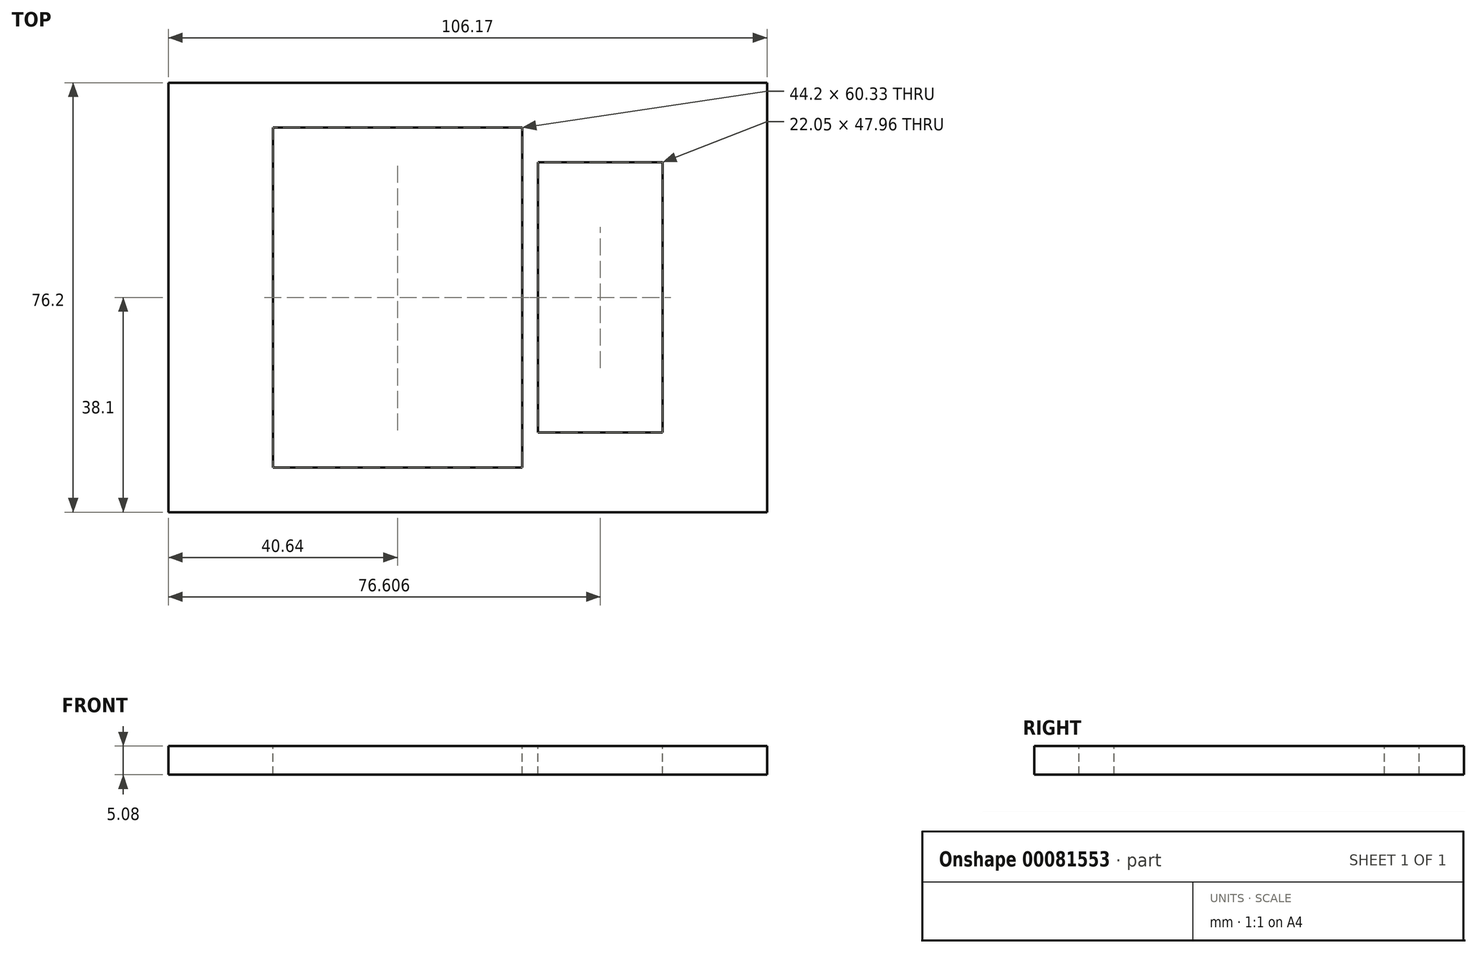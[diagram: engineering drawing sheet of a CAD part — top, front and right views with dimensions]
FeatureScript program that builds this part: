
annotation { "Feature Type Name" : "Feature", "Feature Type Description" : "" }
export const myFeature = defineFeature(function(context is Context, id is Id, definition is map)
    precondition{}
    {
        {
            var Q0;
            Q0=qCreatedBy(makeId("Top.planeOp"),FACE);
            var sketch = newSketch(context, id + "F0", { "sketchPlane" : qUnion([Q0])});
            skLineSegment(sketch, "E0.bottom", {"start": v(0, 0) * mm, "end": v(106.17, 0) * mm});
            skLineSegment(sketch, "E0.top", {"start": v(0, 76.2) * mm, "end": v(106.17, 76.2) * mm});
            skLineSegment(sketch, "E0.left", {"start": v(0, 0) * mm, "end": v(0, 76.2) * mm});
            skLineSegment(sketch, "E0.right", {"start": v(106.17, 0) * mm, "end": v(106.17, 76.2) * mm});
            skSolve(sketch);
        }
        {
            var Q0;
            Q0=makeQuery(id+"F0.imprint","IMPRINT",FACE,{"disambiguationData":[TD([[makeQuery(id+"F0.imprint","IMPRINT",EDGE,{"derivedFrom":sQuery(id+"F0.wireOp",EDGE,"E0.bottom")}),1.0]])]});
            extrude(context, id + "F1", {"entities" : qUnion([Q0]), "depth" : 5.08 * mm});
        }
        {
            var Q0;
            Q0=makeQuery(id+"F1.opExtrude","CAP_FACE",FACE,{"disambiguationData":[OSD([sQuery(id+"F0.wireOp",EDGE,"E0.bottom"),sQuery(id+"F0.wireOp",EDGE,"E0.top"),sQuery(id+"F0.wireOp",EDGE,"E0.left"),sQuery(id+"F0.wireOp",EDGE,"E0.right")])],"isStart":false});
            var sketch = newSketch(context, id + "F2", { "sketchPlane" : qUnion([Q0])});
            skLineSegment(sketch, "E1.bottom", {"start": v(18.54, 68.26) * mm, "end": v(62.74, 68.26) * mm});
            skLineSegment(sketch, "E1.top", {"start": v(18.54, 7.94) * mm, "end": v(62.74, 7.94) * mm});
            skLineSegment(sketch, "E1.left", {"start": v(18.54, 68.26) * mm, "end": v(18.54, 7.94) * mm});
            skLineSegment(sketch, "E1.right", {"start": v(62.74, 68.26) * mm, "end": v(62.74, 7.94) * mm});
            skLineSegment(sketch, "E2", {"start": v(18.54, 38.1) * mm, "end": v(62.74, 38.1) * mm});
            skLineSegment(sketch, "E3.bottom", {"start": v(65.58, 62.08) * mm, "end": v(87.63, 62.08) * mm});
            skLineSegment(sketch, "E3.top", {"start": v(65.58, 14.12) * mm, "end": v(87.63, 14.12) * mm});
            skLineSegment(sketch, "E3.left", {"start": v(65.58, 62.08) * mm, "end": v(65.58, 14.12) * mm});
            skLineSegment(sketch, "E3.right", {"start": v(87.63, 62.08) * mm, "end": v(87.63, 14.12) * mm});
            skLineSegment(sketch, "E4", {"start": v(65.58, 38.1) * mm, "end": v(87.63, 38.1) * mm});
            skSolve(sketch);
        }
        {
            var Q0;
            {var subQ0=sQuery(id+"F2.wireOp",EDGE,"E1.bottom");Q0=makeQuery(id+"F2.imprint","IMPRINT",FACE,{"disambiguationData":[TD([[makeQuery(id+"F2.imprint","IMPRINT",EDGE,{"derivedFrom":subQ0}),-1.0]])]});}
            var Q1;
            {var subQ0=sQuery(id+"F2.wireOp",EDGE,"E1.top");Q1=makeQuery(id+"F2.imprint","IMPRINT",FACE,{"disambiguationData":[TD([[makeQuery(id+"F2.imprint","IMPRINT",EDGE,{"derivedFrom":subQ0}),1.0]])]});}
            var Q2;
            {var subQ0=sQuery(id+"F2.wireOp",EDGE,"E3.bottom");Q2=makeQuery(id+"F2.imprint","IMPRINT",FACE,{"disambiguationData":[TD([[makeQuery(id+"F2.imprint","IMPRINT",EDGE,{"derivedFrom":subQ0}),-1.0]])]});}
            var Q3;
            {var subQ0=sQuery(id+"F2.wireOp",EDGE,"E3.top");Q3=makeQuery(id+"F2.imprint","IMPRINT",FACE,{"disambiguationData":[TD([[makeQuery(id+"F2.imprint","IMPRINT",EDGE,{"derivedFrom":subQ0}),1.0]])]});}
            extrude(context, id + "F3", {"entities" : qUnion([Q0, Q1, Q2, Q3]), "operationType" : NewBodyOperationType.REMOVE, "oppositeDirection" : true, "depth" : 25.4 * mm});
        }
    });
